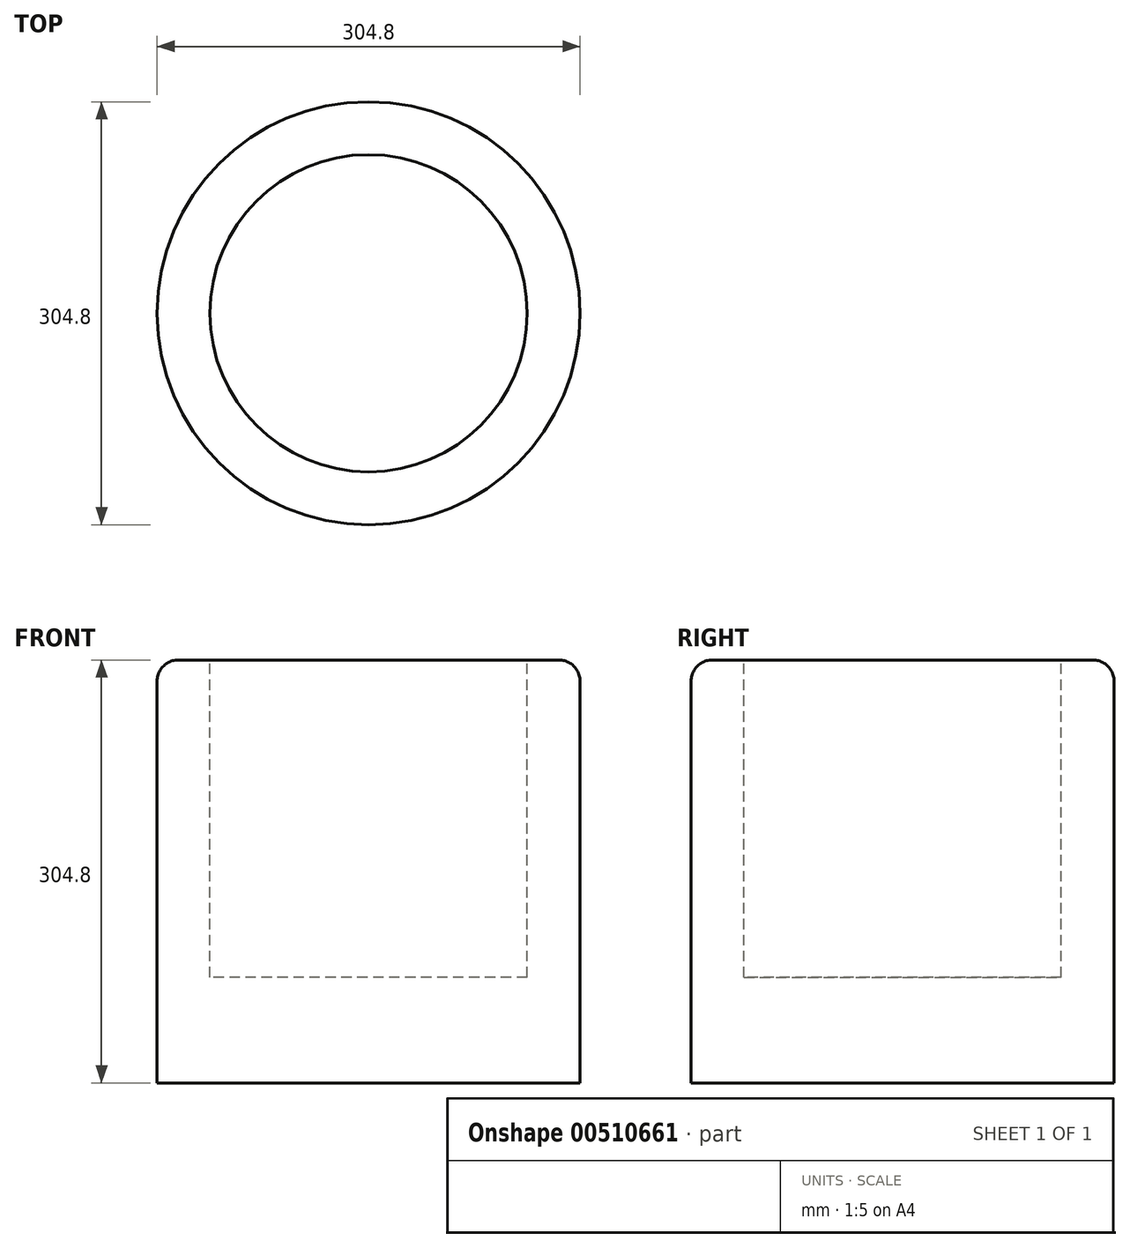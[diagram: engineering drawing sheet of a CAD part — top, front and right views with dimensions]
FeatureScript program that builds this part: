
annotation { "Feature Type Name" : "Feature", "Feature Type Description" : "" }
export const myFeature = defineFeature(function(context is Context, id is Id, definition is map)
    precondition{}
    {
        {
            var Q0;
            Q0=qCreatedBy(makeId("Top.planeOp"),FACE);
            var sketch = newSketch(context, id + "F0", { "sketchPlane" : qUnion([Q0])});
            skCircle(sketch, "E0", {"center": v(-36.68, 40.24) * mm, "radius": 152.4 * mm});
            skSolve(sketch);
        }
        {
            var Q0;
            Q0 = qSketchRegion(id + "F0", true);
            extrude(context, id + "F1", {"entities" : qUnion([Q0]), "depth" : 304.8 * mm, "offsetDistance" : 30.48 * mm});
        }
        {
            var Q0;
            Q0=makeQuery(id+"F1.opExtrude","CAP_FACE",FACE,{"disambiguationData":[OSD([sQuery(id+"F0.wireOp",EDGE,"E0")])],"isStart":false});
            var sketch = newSketch(context, id + "F2", { "sketchPlane" : qUnion([Q0])});
            skCircle(sketch, "E1", {"center": v(-36.68, 40.24) * mm, "radius": 114.3 * mm});
            skSolve(sketch);
        }
        {
            var Q0;
            Q0 = qSketchRegion(id + "F2", true);
            extrude(context, id + "F3", {"entities" : qUnion([Q0]), "operationType" : NewBodyOperationType.REMOVE, "oppositeDirection" : true, "depth" : 228.6 * mm, "offsetDistance" : 30.48 * mm});
        }
        {
            var Q0;
            Q0=makeQuery(id+"F3.boolean.opBoolean","COPY",EDGE,{"derivedFrom":makeQuery(id+"F3.opExtrude","CAP_EDGE",EDGE,{"disambiguationData":[OSD([sQuery(id+"F2.wireOp",EDGE,"E1")])],"isStart":true})});
            var Q1;
            Q1=makeQuery(id+"F1.opExtrude","CAP_EDGE",EDGE,{"disambiguationData":[OSD([sQuery(id+"F0.wireOp",EDGE,"E0")])],"isStart":false});
            fillet(context, id + "F4", {"entities" : qUnion([Q0, Q1]), "radius" : 15.24 * mm, "tangentPropagation" : true, "allowEdgeOverflow" : false});
        }
    });
